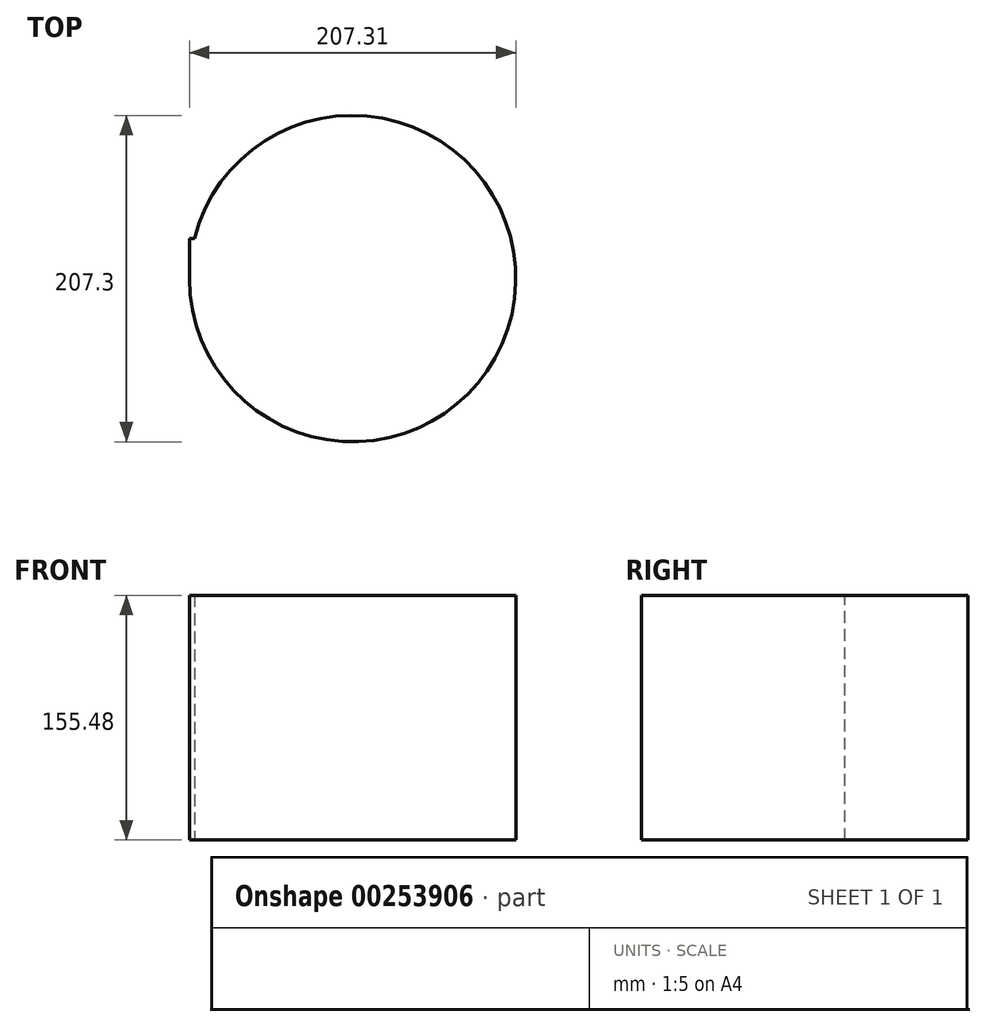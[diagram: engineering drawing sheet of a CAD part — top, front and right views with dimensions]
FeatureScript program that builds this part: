
annotation { "Feature Type Name" : "Feature", "Feature Type Description" : "" }
export const myFeature = defineFeature(function(context is Context, id is Id, definition is map)
    precondition{}
    {
        {
            var Q0;
            Q0=qCreatedBy(makeId("Front.planeOp"),FACE);
            var sketch = newSketch(context, id + "F0", { "sketchPlane" : qUnion([Q0])});
            skLineSegment(sketch, "E0.bottom", {"start": v(0, -35.25) * mm, "end": v(0, 120.23) * mm});
            skLineSegment(sketch, "E0.top", {"start": v(103.65, -35.25) * mm, "end": v(103.65, 120.23) * mm});
            skLineSegment(sketch, "E0.left", {"start": v(0, -35.25) * mm, "end": v(103.65, -35.25) * mm});
            skLineSegment(sketch, "E0.right", {"start": v(0, 120.23) * mm, "end": v(103.65, 120.23) * mm});
            skPoint(sketch, "E0.middle", {"position": v(51.83, 42.49) * mm});
            skSolve(sketch);
        }
        {
            var Q0;
            Q0=makeQuery(id+"F0.imprint","IMPRINT",FACE,{"disambiguationData":[TD([[makeQuery(id+"F0.imprint","IMPRINT",EDGE,{"derivedFrom":sQuery(id+"F0.wireOp",EDGE,"E0.bottom")}),-1.0]])]});
            extrude(context, id + "F1", {"entities" : qUnion([Q0]), "depth" : 25.4 * mm});
        }
        {
            var Q0;
            Q0=makeQuery(id+"F1.opExtrude","CAP_FACE",FACE,{"disambiguationData":[OSD([sQuery(id+"F0.wireOp",EDGE,"E0.bottom"),sQuery(id+"F0.wireOp",EDGE,"E0.top"),sQuery(id+"F0.wireOp",EDGE,"E0.left"),sQuery(id+"F0.wireOp",EDGE,"E0.right")])],"isStart":false});
            var Q1;
            Q1=makeQuery(id+"F1.opExtrude","CAP_EDGE",EDGE,{"disambiguationData":[OSD([sQuery(id+"F0.wireOp",EDGE,"E0.top")])],"isStart":false});
            revolve(context, id + "F2", {"operationType" : NewBodyOperationType.ADD, "entities" : qUnion([Q0]), "axis" : qUnion([Q1]), "revolveType" : RevolveType.FULL});
        }
    });
